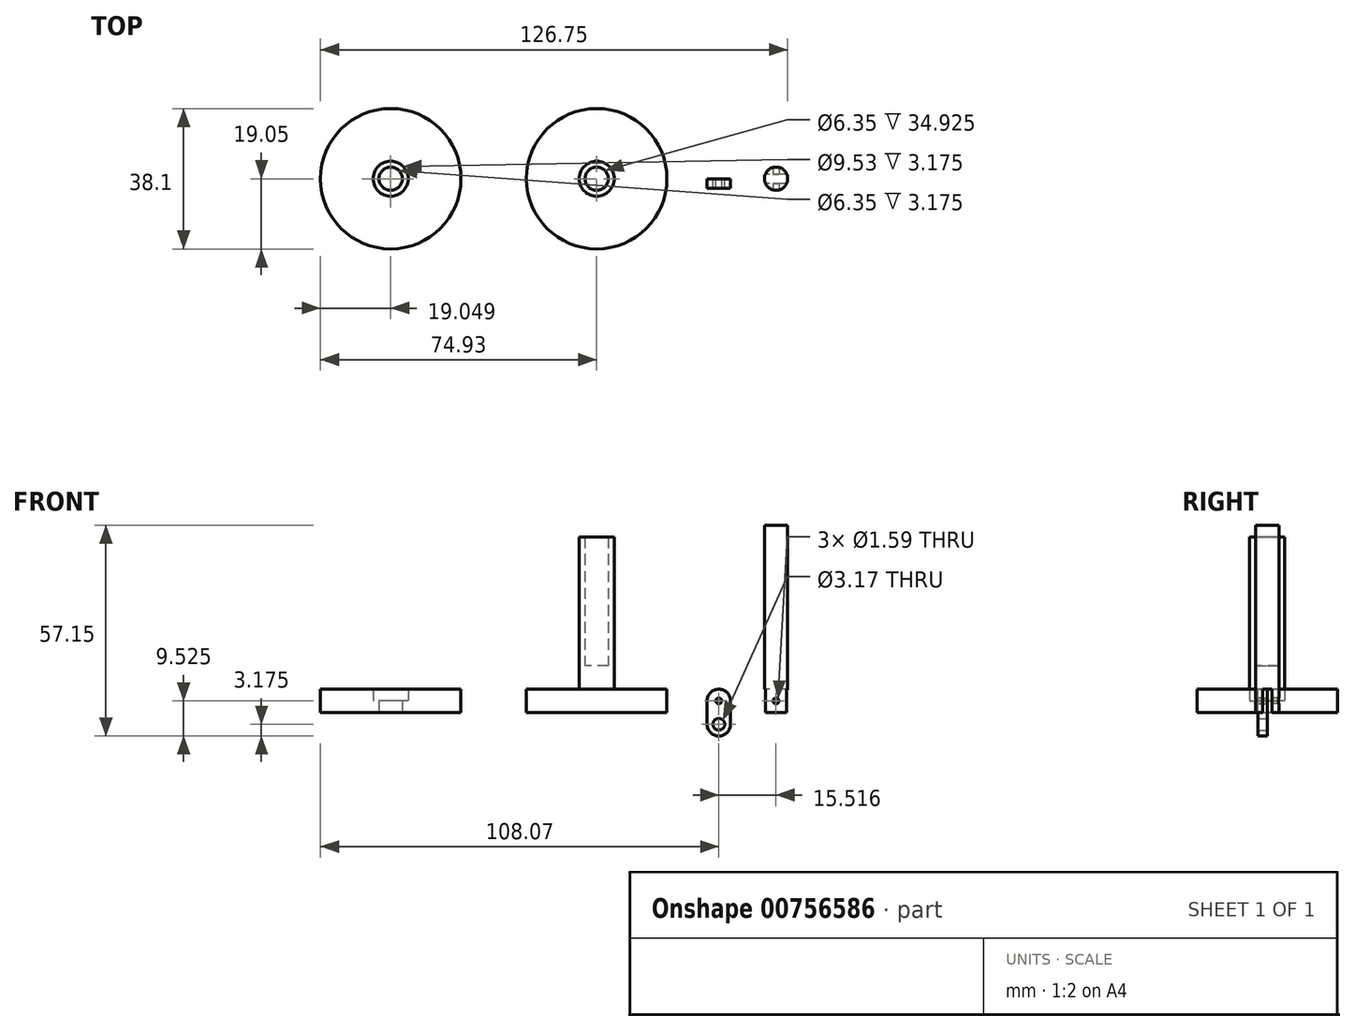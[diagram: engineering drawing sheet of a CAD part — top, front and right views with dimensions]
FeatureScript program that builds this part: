
annotation { "Feature Type Name" : "Feature", "Feature Type Description" : "" }
export const myFeature = defineFeature(function(context is Context, id is Id, definition is map)
    precondition{}
    {
        {
            var Q0;
            Q0=qCreatedBy(makeId("Top.planeOp"),FACE);
            var sketch = newSketch(context, id + "F0", { "sketchPlane" : qUnion([Q0])});
            skCircle(sketch, "E0", {"center": v(0, 0) * mm, "radius": 19.05 * mm});
            skCircle(sketch, "E1", {"center": v(0, 0) * mm, "radius": 3.18 * mm});
            skCircle(sketch, "E2", {"center": v(0, 0) * mm, "radius": 4.76 * mm});
            skSolve(sketch);
        }
        {
            var Q0;
            Q0=makeQuery(id+"F0.imprint","IMPRINT",FACE,{"disambiguationData":[TD([[makeQuery(id+"F0.imprint","IMPRINT",EDGE,{"derivedFrom":sQuery(id+"F0.wireOp",EDGE,"E0")}),1.0]])]});
            extrude(context, id + "F1", {"entities" : qUnion([Q0]), "depth" : 6.35 * mm, "offsetDistance" : 25.4 * mm});
        }
        {
            var Q0;
            Q0=makeQuery(id+"F0.imprint","IMPRINT",FACE,{"disambiguationData":[TD([[makeQuery(id+"F0.imprint","IMPRINT",EDGE,{"derivedFrom":sQuery(id+"F0.wireOp",EDGE,"E1")}),1.0]])]});
            extrude(context, id + "F2", {"entities" : qUnion([Q0]), "operationType" : NewBodyOperationType.ADD, "depth" : 12.7 * mm, "offsetDistance" : 25.4 * mm});
        }
        {
            var Q0;
            Q0=makeQuery(id+"F0.imprint","IMPRINT",FACE,{"disambiguationData":[TD([[makeQuery(id+"F0.imprint","IMPRINT",EDGE,{"derivedFrom":sQuery(id+"F0.wireOp",EDGE,"E1")}),-1.0]])]});
            extrude(context, id + "F3", {"entities" : qUnion([Q0]), "operationType" : NewBodyOperationType.ADD, "depth" : 47.62 * mm, "offsetDistance" : 25.4 * mm});
        }
        {
            var Q0;
            Q0=qCreatedBy(makeId("Top.planeOp"),FACE);
            var sketch = newSketch(context, id + "F4", { "sketchPlane" : qUnion([Q0])});
            skPoint(sketch, "E3", {"position": v(-55.88, 0) * mm});
            skCircle(sketch, "E4", {"center": v(-55.88, 0) * mm, "radius": 19.05 * mm});
            skCircle(sketch, "E5", {"center": v(-55.88, 0) * mm, "radius": 4.76 * mm});
            skCircle(sketch, "E6", {"center": v(-55.88, 0) * mm, "radius": 3.18 * mm});
            skSolve(sketch);
        }
        {
            var Q0;
            Q0=makeQuery(id+"F4.imprint","IMPRINT",FACE,{"disambiguationData":[TD([[makeQuery(id+"F4.imprint","IMPRINT",EDGE,{"derivedFrom":sQuery(id+"F4.wireOp",EDGE,"E4")}),1.0]])]});
            extrude(context, id + "F5", {"entities" : qUnion([Q0]), "depth" : 6.35 * mm, "offsetDistance" : 25.4 * mm});
        }
        {
            var Q0;
            Q0=makeQuery(id+"F4.imprint","IMPRINT",FACE,{"disambiguationData":[TD([[makeQuery(id+"F4.imprint","IMPRINT",EDGE,{"derivedFrom":sQuery(id+"F4.wireOp",EDGE,"E5")}),1.0]])]});
            extrude(context, id + "F6", {"entities" : qUnion([Q0]), "operationType" : NewBodyOperationType.ADD, "depth" : 3.17 * mm, "offsetDistance" : 25.4 * mm});
        }
        {
            var Q0;
            Q0=qCreatedBy(makeId("Top.planeOp"),FACE);
            var sketch = newSketch(context, id + "F7", { "sketchPlane" : qUnion([Q0])});
            skPoint(sketch, "E7", {"position": v(48.66, 0) * mm});
            skCircle(sketch, "E8", {"center": v(48.66, 0) * mm, "radius": 3.16 * mm});
            skLineSegment(sketch, "E9", {"start": v(48.66, 0) * mm, "end": v(45.5, 0) * mm});
            skLineSegment(sketch, "E10", {"start": v(48.66, 0) * mm, "end": v(51.82, 0) * mm});
            skLineSegment(sketch, "E11", {"start": v(48.66, 1.27) * mm, "end": v(48.66, 0) * mm});
            skLineSegment(sketch, "E12", {"start": v(48.66, 0) * mm, "end": v(48.66, -1.27) * mm});
            skLineSegment(sketch, "E13", {"start": v(48.66, 1.27) * mm, "end": v(45.76, 1.27) * mm});
            skLineSegment(sketch, "E14", {"start": v(48.66, 1.27) * mm, "end": v(51.55, 1.27) * mm});
            skLineSegment(sketch, "E15", {"start": v(48.66, -1.27) * mm, "end": v(45.76, -1.27) * mm});
            skLineSegment(sketch, "E16", {"start": v(48.66, -1.27) * mm, "end": v(51.55, -1.27) * mm});
            skSolve(sketch);
        }
        {
            var Q0;
            Q0 = qSketchRegion(id + "F7", true);
            extrude(context, id + "F8", {"entities" : qUnion([Q0]), "depth" : 50.8 * mm, "offsetDistance" : 25.4 * mm});
        }
        {
            var Q0;
            {var subQ0=sQuery(id+"F7.wireOp",EDGE,"E9");Q0=makeQuery(id+"F7.imprint","IMPRINT",FACE,{"disambiguationData":[TD([[makeQuery(id+"F7.imprint","IMPRINT",EDGE,{"derivedFrom":subQ0}),-1.0]])]});}
            var Q1;
            {var subQ0=sQuery(id+"F7.wireOp",EDGE,"E10");Q1=makeQuery(id+"F7.imprint","IMPRINT",FACE,{"disambiguationData":[TD([[makeQuery(id+"F7.imprint","IMPRINT",EDGE,{"derivedFrom":subQ0}),1.0]])]});}
            var Q2;
            {var subQ0=sQuery(id+"F7.wireOp",EDGE,"E9");Q2=makeQuery(id+"F7.imprint","IMPRINT",FACE,{"disambiguationData":[TD([[makeQuery(id+"F7.imprint","IMPRINT",EDGE,{"derivedFrom":subQ0}),1.0]])]});}
            var Q3;
            {var subQ0=sQuery(id+"F7.wireOp",EDGE,"E10");Q3=makeQuery(id+"F7.imprint","IMPRINT",FACE,{"disambiguationData":[TD([[makeQuery(id+"F7.imprint","IMPRINT",EDGE,{"derivedFrom":subQ0}),-1.0]])]});}
            extrude(context, id + "F9", {"entities" : qUnion([Q0, Q1, Q2, Q3]), "operationType" : NewBodyOperationType.REMOVE, "depth" : 6.35 * mm, "offsetDistance" : 25.4 * mm});
        }
        {
            var Q0;
            Q0=qCreatedBy(makeId("Front.planeOp"),FACE);
            var sketch = newSketch(context, id + "F10", { "sketchPlane" : qUnion([Q0])});
            skLineSegment(sketch, "E17", {"start": v(48.66, 0) * mm, "end": v(48.66, 3.18) * mm, "construction": true});
            skCircle(sketch, "E18", {"center": v(48.66, 3.18) * mm, "radius": 0.8 * mm});
            skSolve(sketch);
        }
        {
            var Q0;
            Q0=makeQuery(id+"F10.imprint","IMPRINT",FACE,{"disambiguationData":[TD([[makeQuery(id+"F10.imprint","IMPRINT",EDGE,{"derivedFrom":sQuery(id+"F10.wireOp",EDGE,"E18")}),1.0]])]});
            extrude(context, id + "F11", {"entities" : qUnion([Q0]), "operationType" : NewBodyOperationType.REMOVE, "oppositeDirection" : true, "depth" : 3.17 * mm, "offsetDistance" : 25.4 * mm, "hasSecondDirection" : true, "secondDirectionOppositeDirection" : false, "secondDirectionDepth" : 3.17 * mm});
        }
        {
            var Q0;
            Q0=qCreatedBy(makeId("Front.planeOp"),FACE);
            var sketch = newSketch(context, id + "F12", { "sketchPlane" : qUnion([Q0])});
            skPoint(sketch, "E19", {"position": v(33.14, 0) * mm});
            skPoint(sketch, "E20", {"position": v(33.14, 3.18) * mm});
            skCircle(sketch, "E21", {"center": v(33.14, 3.18) * mm, "radius": 0.8 * mm});
            skCircle(sketch, "E22", {"center": v(33.14, 3.18) * mm, "radius": 3.18 * mm});
            skPoint(sketch, "E23", {"position": v(33.14, -3.18) * mm});
            skCircle(sketch, "E24", {"center": v(33.14, -3.18) * mm, "radius": 1.59 * mm});
            skCircle(sketch, "E25", {"center": v(33.14, -3.18) * mm, "radius": 3.17 * mm});
            skLineSegment(sketch, "E26", {"start": v(29.97, -3.18) * mm, "end": v(29.97, 3.18) * mm});
            skLineSegment(sketch, "E27", {"start": v(36.32, -3.18) * mm, "end": v(36.32, 3.18) * mm});
            skSolve(sketch);
        }
        {
            var Q0;
            Q0 = qSketchRegion(id + "F12", true);
            extrude(context, id + "F13", {"entities" : qUnion([Q0]), "depth" : 2.54 * mm, "offsetDistance" : 25.4 * mm});
        }
    });
